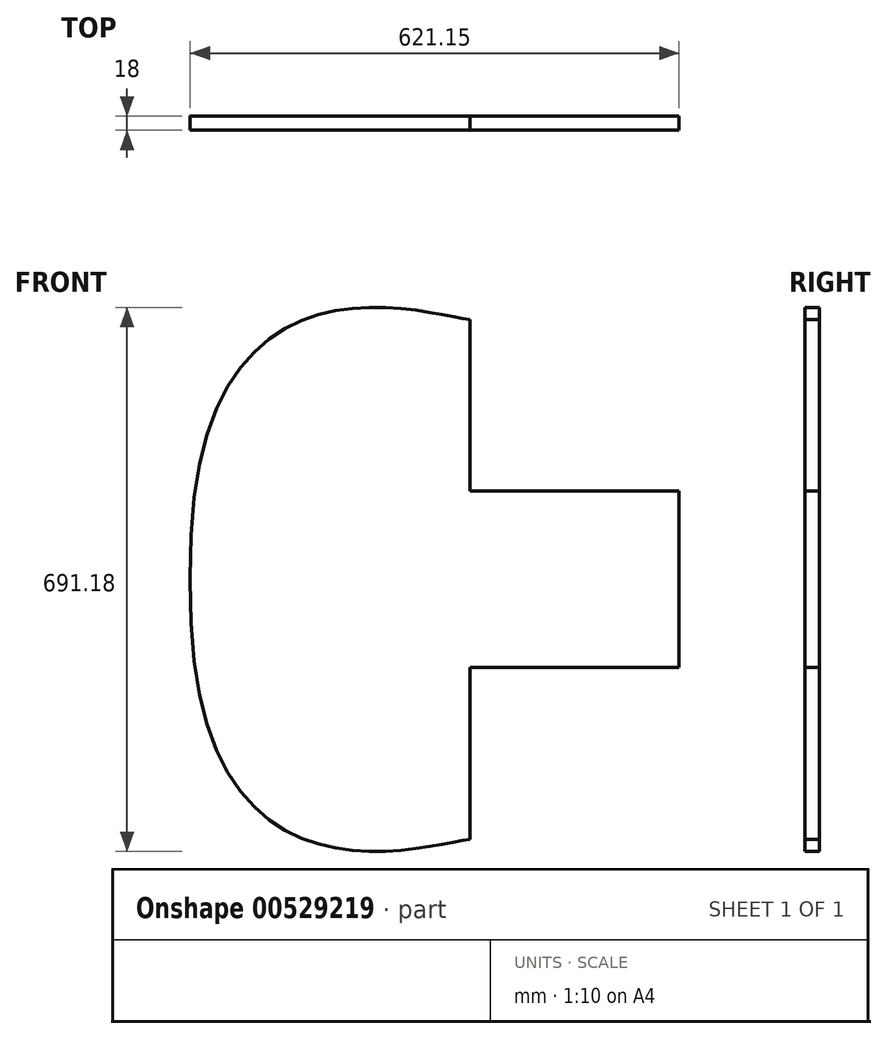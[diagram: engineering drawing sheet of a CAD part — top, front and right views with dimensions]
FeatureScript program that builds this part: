
annotation { "Feature Type Name" : "Feature", "Feature Type Description" : "" }
export const myFeature = defineFeature(function(context is Context, id is Id, definition is map)
    precondition{}
    {
        {
            var Q0;
            Q0=qCreatedBy(makeId("Front.planeOp"),FACE);
            var sketch = newSketch(context, id + "F0", { "sketchPlane" : qUnion([Q0])});
            skLineSegment(sketch, "E0", {"start": v(-355.6, 0) * mm, "end": v(355.6, 0) * mm, "construction": true});
            skLineSegment(sketch, "E1.0.1.0", {"start": v(-355.6, 50.8) * mm, "end": v(355.6, 50.8) * mm, "construction": true});
            skLineSegment(sketch, "E1.0.2.0", {"start": v(-355.6, 101.6) * mm, "end": v(355.6, 101.6) * mm, "construction": true});
            skLineSegment(sketch, "E1.0.3.0", {"start": v(-355.6, 152.4) * mm, "end": v(355.6, 152.4) * mm, "construction": true});
            skLineSegment(sketch, "E1.0.4.0", {"start": v(-355.6, 203.2) * mm, "end": v(355.6, 203.2) * mm, "construction": true});
            skLineSegment(sketch, "E1.0.5.0", {"start": v(-355.6, 254) * mm, "end": v(355.6, 254) * mm, "construction": true});
            skLineSegment(sketch, "E1.direction1", {"start": v(-355.6, 0) * mm, "end": v(-330.6, 0) * mm, "construction": true});
            skLineSegment(sketch, "E1.direction2", {"start": v(-355.6, 0) * mm, "end": v(-355.6, 50.8) * mm, "construction": true});
            skLineSegment(sketch, "E2.0.1.0", {"start": v(-355.6, -50.8) * mm, "end": v(355.6, -50.8) * mm, "construction": true});
            skLineSegment(sketch, "E2.0.2.0", {"start": v(-355.6, -101.6) * mm, "end": v(355.6, -101.6) * mm, "construction": true});
            skLineSegment(sketch, "E2.0.3.0", {"start": v(-355.6, -152.4) * mm, "end": v(355.6, -152.4) * mm, "construction": true});
            skLineSegment(sketch, "E2.0.4.0", {"start": v(-355.6, -203.2) * mm, "end": v(355.6, -203.2) * mm, "construction": true});
            skLineSegment(sketch, "E2.0.5.0", {"start": v(-355.6, -254) * mm, "end": v(355.6, -254) * mm, "construction": true});
            skLineSegment(sketch, "E2.direction1", {"start": v(-355.6, 0) * mm, "end": v(0, 0) * mm, "construction": true});
            skLineSegment(sketch, "E2.direction2", {"start": v(-355.6, 0) * mm, "end": v(-355.6, -50.8) * mm, "construction": true});
            skLineSegment(sketch, "E3", {"start": v(0, 254) * mm, "end": v(0, -254) * mm, "construction": true});
            skLineSegment(sketch, "E4.1.0.0", {"start": v(50.8, 254) * mm, "end": v(50.8, -254) * mm, "construction": true});
            skLineSegment(sketch, "E4.2.0.0", {"start": v(101.6, 254) * mm, "end": v(101.6, -254) * mm, "construction": true});
            skLineSegment(sketch, "E4.3.0.0", {"start": v(152.4, 254) * mm, "end": v(152.4, -254) * mm, "construction": true});
            skLineSegment(sketch, "E4.4.0.0", {"start": v(203.2, 254) * mm, "end": v(203.2, -254) * mm, "construction": true});
            skLineSegment(sketch, "E4.5.0.0", {"start": v(254, 254) * mm, "end": v(254, -254) * mm, "construction": true});
            skLineSegment(sketch, "E4.6.0.0", {"start": v(304.8, 254) * mm, "end": v(304.8, -254) * mm, "construction": true});
            skLineSegment(sketch, "E4.7.0.0", {"start": v(355.6, 254) * mm, "end": v(355.6, -254) * mm, "construction": true});
            skLineSegment(sketch, "E4.direction1", {"start": v(0, -254) * mm, "end": v(50.8, -254) * mm, "construction": true});
            skLineSegment(sketch, "E5.1.0.0", {"start": v(-50.8, 254) * mm, "end": v(-50.8, -254) * mm, "construction": true});
            skLineSegment(sketch, "E5.2.0.0", {"start": v(-101.6, 254) * mm, "end": v(-101.6, -254) * mm, "construction": true});
            skLineSegment(sketch, "E5.3.0.0", {"start": v(-152.4, 254) * mm, "end": v(-152.4, -254) * mm, "construction": true});
            skLineSegment(sketch, "E5.4.0.0", {"start": v(-203.2, 254) * mm, "end": v(-203.2, -254) * mm, "construction": true});
            skLineSegment(sketch, "E5.5.0.0", {"start": v(-254, 254) * mm, "end": v(-254, -254) * mm, "construction": true});
            skLineSegment(sketch, "E5.6.0.0", {"start": v(-304.8, 254) * mm, "end": v(-304.8, -254) * mm, "construction": true});
            skLineSegment(sketch, "E5.7.0.0", {"start": v(-355.6, 254) * mm, "end": v(-355.6, -254) * mm, "construction": true});
            skLineSegment(sketch, "E5.direction1", {"start": v(0, -254) * mm, "end": v(-50.8, -254) * mm, "construction": true});
            skLineSegment(sketch, "E6", {"start": v(-326, -217) * mm, "end": v(295, -217) * mm});
            skLineSegment(sketch, "E7", {"start": v(295, -217) * mm, "end": v(295, -105) * mm});
            skLineSegment(sketch, "E8", {"start": v(295, -105) * mm, "end": v(29, -105) * mm});
            skLineSegment(sketch, "E9", {"start": v(29, -105) * mm, "end": v(29, 113) * mm});
            skFitSpline(sketch, "E10", {"points": [v(29, 113) * mm, v(-326, -217) * mm], "startDerivative": vector(-184.14, 24.08) * mm, "endDerivative": vector(23.26, -1317.35) * mm});
            skFitSpline(sketch, "E11.MirrorCS", {"points": [v(29, -547) * mm, v(-326, -217) * mm], "startDerivative": vector(-184.14, -24.08) * mm, "endDerivative": vector(23.26, 1317.35) * mm});
            skLineSegment(sketch, "E12.MirrorCS", {"start": v(29, -329) * mm, "end": v(29, -547) * mm});
            skLineSegment(sketch, "E13.MirrorCS", {"start": v(295, -329) * mm, "end": v(29, -329) * mm});
            skLineSegment(sketch, "E14.MirrorCS", {"start": v(295, -217) * mm, "end": v(295, -329) * mm});
            skSolve(sketch);
        }
        {
            var Q0;
            Q0=makeQuery(id+"F0.imprint","IMPRINT",FACE,{"disambiguationData":[TD([[makeQuery(id+"F0.imprint","IMPRINT",EDGE,{"derivedFrom":sQuery(id+"F0.wireOp",EDGE,"E6")}),-1.0]])]});
            var Q1;
            Q1=makeQuery(id+"F0.imprint","IMPRINT",FACE,{"disambiguationData":[TD([[makeQuery(id+"F0.imprint","IMPRINT",EDGE,{"derivedFrom":sQuery(id+"F0.wireOp",EDGE,"E6")}),1.0]])]});
            extrude(context, id + "F1", {"entities" : qUnion([Q0, Q1]), "depth" : 18 * mm, "offsetDistance" : 25 * mm});
        }
        {
            var Q0;
            Q0=makeQuery(id+"F1.opExtrude","SWEPT_EDGE",EDGE,{"disambiguationData":[OSD([sQuery(id+"F0.wireOp",EDGE,"E6"),sQuery(id+"F0.wireOp",EDGE,"E10"),sQuery(id+"F0.wireOp",EDGE,"E11.MirrorCS")])]});
            fillet(context, id + "F2", {"entities" : qUnion([Q0]), "radius" : 100 * mm, "tangentPropagation" : true, "allowEdgeOverflow" : false});
        }
    });
